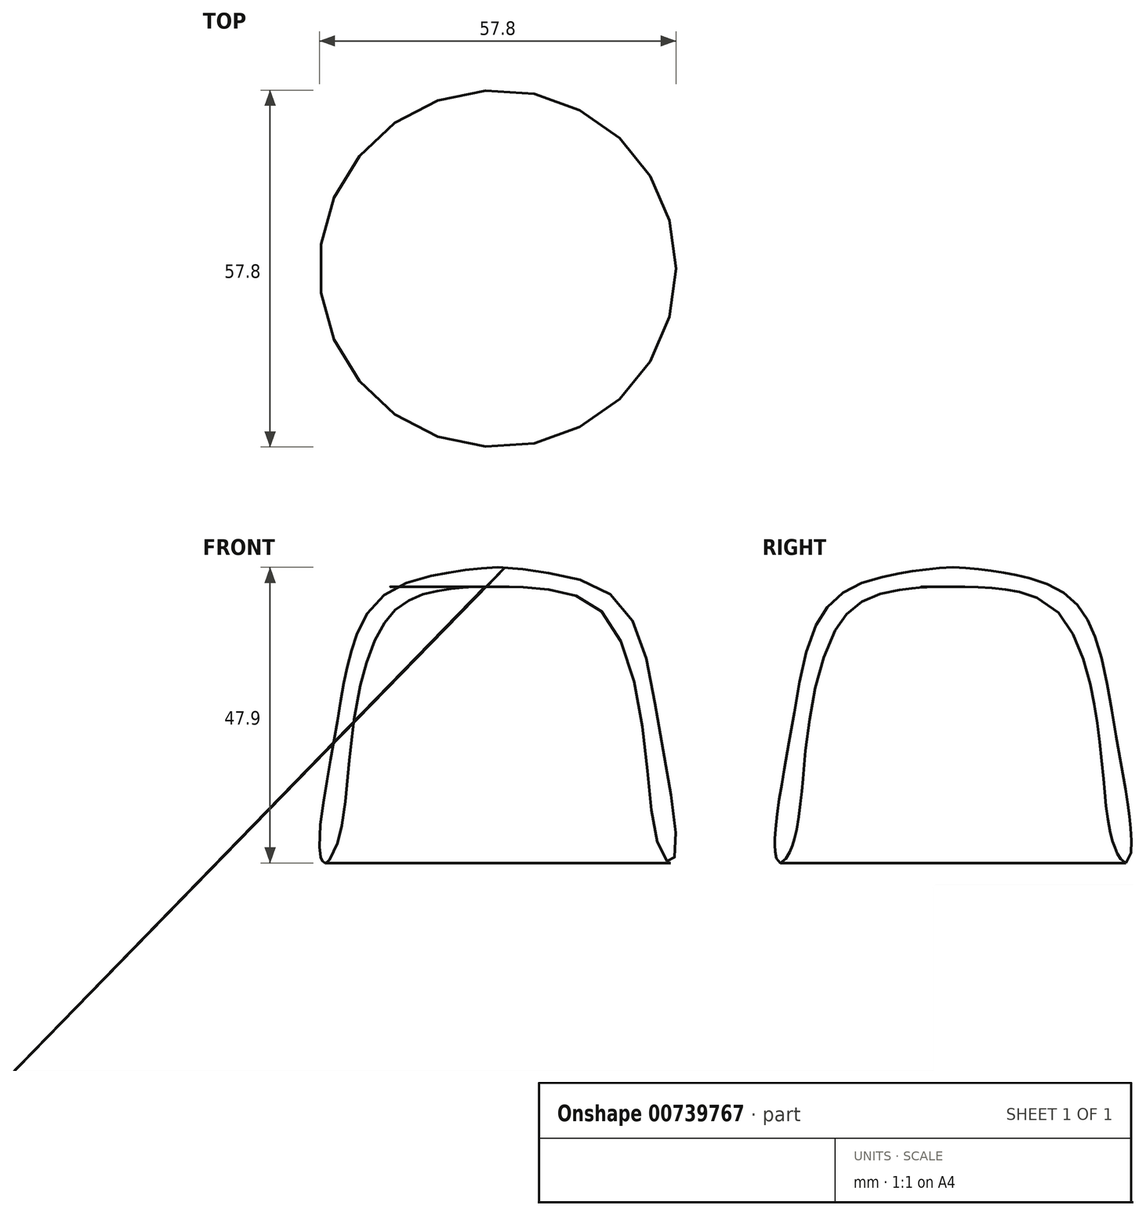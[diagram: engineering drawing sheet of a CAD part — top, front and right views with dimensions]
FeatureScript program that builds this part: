
annotation { "Feature Type Name" : "Feature", "Feature Type Description" : "" }
export const myFeature = defineFeature(function(context is Context, id is Id, definition is map)
    precondition{}
    {
        {
            var Q0;
            Q0=qCreatedBy(makeId("Front.planeOp"),FACE);
            var sketch = newSketch(context, id + "F0", { "sketchPlane" : qUnion([Q0])});
            skFitSpline(sketch, "E0", {"points": [v(0, 47.9) * mm, v(7.86, 47.05) * mm, v(19.7, 42.3) * mm, v(26.07, 22.5) * mm, v(28.9, 2.62) * mm, v(28.01, 0) * mm, v(25.9, 3.32) * mm, v(23.6, 20.9) * mm, v(17.06, 40.53) * mm, v(7.94, 44.37) * mm, v(0, 44.73) * mm], "startDerivative": vector(99.94, -2.94) * mm, "endDerivative": vector(-100.15, -3.13) * mm});
            skLineSegment(sketch, "E1", {"start": v(0, 47.9) * mm, "end": v(0, 44.73) * mm});
            skSolve(sketch);
        }
        {
            var Q0;
            Q0=qCreatedBy(makeId("Front.planeOp"),FACE);
            var sketch = newSketch(context, id + "F1", { "sketchPlane" : qUnion([Q0])});
            skLineSegment(sketch, "E2", {"start": v(0, 71.05) * mm, "end": v(0, -42.77) * mm});
            skSolve(sketch);
        }
        {
            var Q0;
            Q0=makeQuery(id+"F0.imprint","IMPRINT",FACE,{"disambiguationData":[TD([[makeQuery(id+"F0.imprint","IMPRINT",EDGE,{"derivedFrom":sQuery(id+"F0.wireOp",EDGE,"E0")}),-1.0]])]});
            var Q1;
            Q1=sQuery(id+"F1.wireOp",EDGE,"E2");
            revolve(context, id + "F2", {"surfaceOperationType" : NewSurfaceOperationType.NEW, "entities" : qUnion([Q0]), "axis" : qUnion([Q1]), "revolveType" : RevolveType.FULL});
        }
    });
